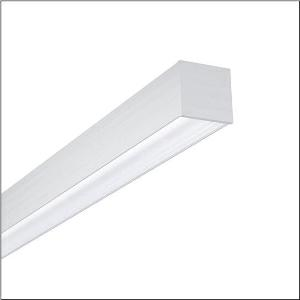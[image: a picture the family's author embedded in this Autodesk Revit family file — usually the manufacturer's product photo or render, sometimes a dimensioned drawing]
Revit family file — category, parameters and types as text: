
# Revit family: silica_r_5mx21bd1e4a_4ae4
name_source: partatom
category: Lighting Fixtures
units: mm (PartAtom-declared; Revit-internal decimal feet)

## family parameters
Cut with Voids When Loaded = No
Host = Face
Light Source = No
Part Type = Normal
Room Calculation Point = No
Round Connector Dimension = Use Diameter
Shared = No

## types (1)
- --- (1 x LED, 4950 lm, 29.3 W, 4000K)
    Apparent Load = 29 VA
    CIE Flux Codes = 82 97 100 100 100
    Color Rendering = 80
    Color Temperature = 4000K
    Default Elevation = 1800 mm
    Description = Silica®, office luminaire, of aluminium, light emission: direct distribution, primary light characteristic: symmetric, installation type: surface-mounted, LED, rated luminous flux: 4.950lm, luminous efficacy: 169lm/W, light colour: 840, colour temperature: 4000K, control gear: ECG DALI, with terminal, 3+2-pole, max. 2.5mm², mains connection: 230V, AC, 50/60Hz, rated input power: 29W, luminaire housing, of aluminium, anodised, silver, length: 1.442mm, width: 65mm, height: 64mm, protection rating (complete): IP20, insulation class (complete): insulation class I (protective earthing), certification: CE, permissible operating ambient temperature: 0..+35°C, standard: EN 50419, packaging unit: 1 piece
    Height = 64 mm
    Lamp = 1 x LED
    Lamp Light Flux = 4950 lm
    Lamp Power = 29.3 W
    Lamp count = 1
    Length = 1442 mm
    Luminous efficacy = 169 lm/W
    Manufacturer = Siteco
    ModVariant = No
    Model = 5MX21BD1E4A
    Mounting Place = Ceiling
    Mounting Type = Surface mounted
    Number of Poles = 1
    OnlyDefault = Yes
    Power Factor = 1
    Product Name = Silica®
    Product group = office luminaire | ceiling mounted
    ProductGroupID = 304
    Protection Class = Protection class I
    Protection Degree = IP 20
    RLX_Detail_Level = 1
    RLX_Emergency_Light_Flux = 0 lm
    RLX_Emergency_Type = 0
    RLX_Emergency_Type_DB = No
    RlxData = <blob elided: 27249 chars, md5=cdc4a0ac>
    Socket = socket
    Standby Power = 0 W
    System Light Flux = 4950 lm
    System Power = 29 W
    Type Comments = factory setting: luminous flux: 100 % | dim-lin: 254 | 163 mA
    Type Image = l_1004827.jpg
    URL = http://relux.com
    VarID = @adj_138722
    Voltage = 0 V
    Weight = 0.00 kg
    Width = 66 mm

## geometry (parser evidence)
native form markers: Blend x4, Sweep x10
no freeform markers — native parametric forms only
